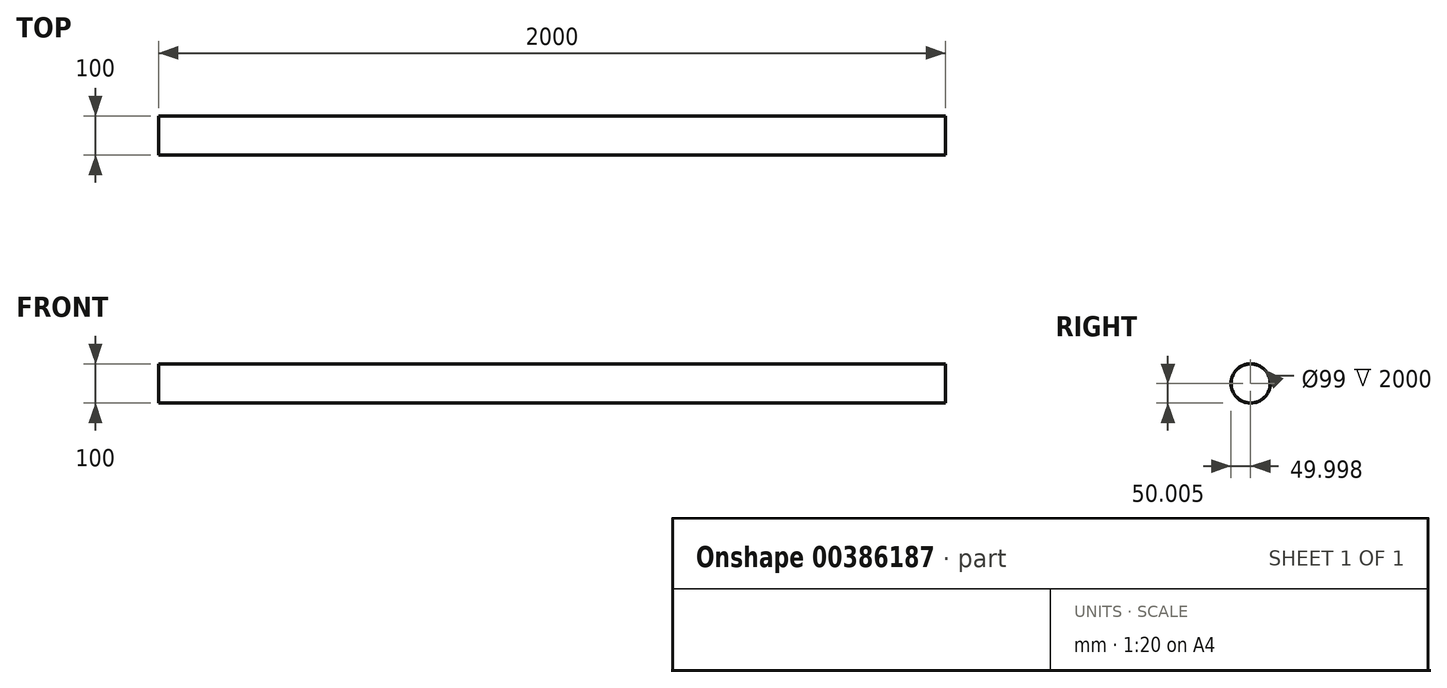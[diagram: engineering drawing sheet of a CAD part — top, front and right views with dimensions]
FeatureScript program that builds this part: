
annotation { "Feature Type Name" : "Feature", "Feature Type Description" : "" }
export const myFeature = defineFeature(function(context is Context, id is Id, definition is map)
    precondition{}
    {
        {
            var Q0;
            Q0=qCreatedBy(makeId("Right.planeOp"),FACE);
            var sketch = newSketch(context, id + "F0", { "sketchPlane" : qUnion([Q0])});
            skCircle(sketch, "E0", {"center": v(-5.26, 4.35) * mm, "radius": 50 * mm});
            skCircle(sketch, "E1", {"center": v(-5.26, 4.35) * mm, "radius": 49.5 * mm});
            skSolve(sketch);
        }
        {
            var Q0;
            Q0 = qSketchRegion(id + "F0", true);
            extrude(context, id + "F1", {"entities" : qUnion([Q0]), "depth" : 2000 * mm});
        }
    });
